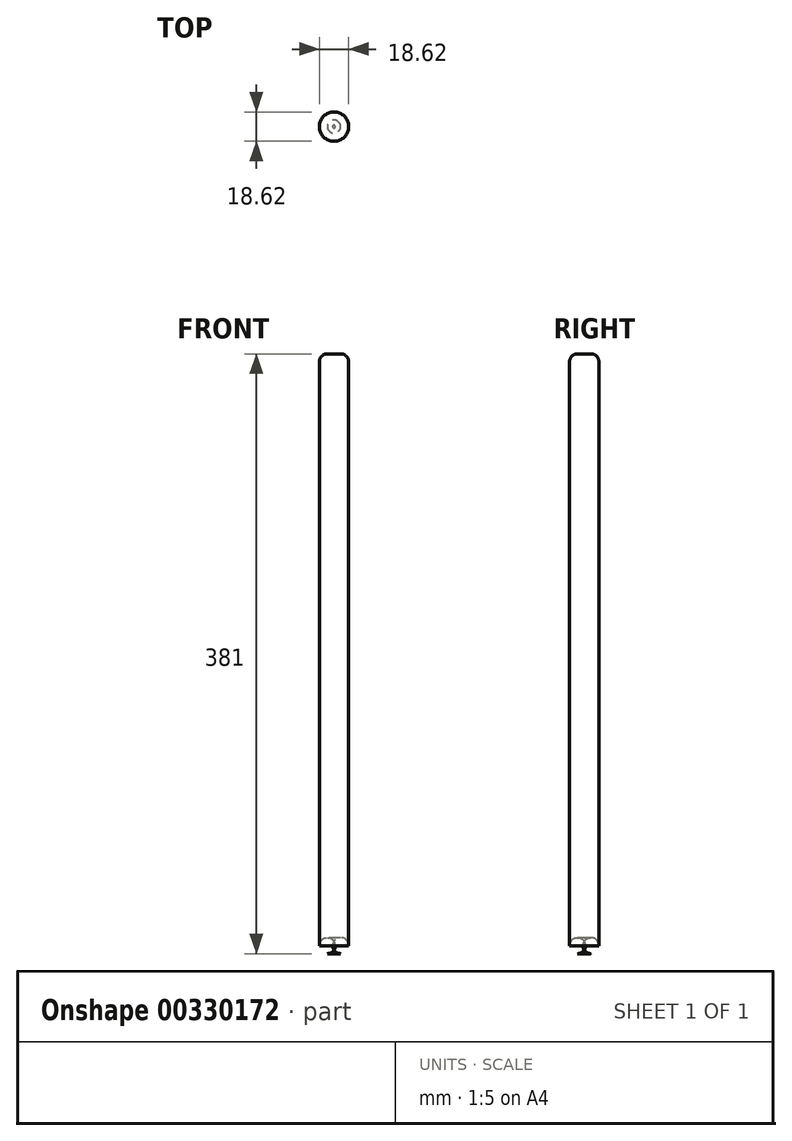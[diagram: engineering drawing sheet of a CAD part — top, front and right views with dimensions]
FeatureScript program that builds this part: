
annotation { "Feature Type Name" : "Feature", "Feature Type Description" : "" }
export const myFeature = defineFeature(function(context is Context, id is Id, definition is map)
    precondition{}
    {
        {
            var Q0;
            Q0=qCreatedBy(makeId("Top.planeOp"),FACE);
            var sketch = newSketch(context, id + "F0", { "sketchPlane" : qUnion([Q0])});
            skPoint(sketch, "E0", {"position": v(0, 0) * mm});
            skCircle(sketch, "E1", {"center": v(0, 0) * mm, "radius": 9.3 * mm});
            skSolve(sketch);
        }
        {
            var Q0;
            Q0 = qSketchRegion(id + "F0", true);
            extrude(context, id + "F1", {"entities" : qUnion([Q0]), "depth" : 381 * mm});
        }
        {
            var Q0;
            Q0=makeQuery(id+"F1.opExtrude","CAP_EDGE",EDGE,{"disambiguationData":[OSD([sQuery(id+"F0.wireOp",EDGE,"E1")])],"isStart":true});
            fillet(context, id + "F2", {"entities" : qUnion([Q0]), "radius" : 5.08 * mm, "tangentPropagation" : true, "allowEdgeOverflow" : false});
        }
        {
            var Q0;
            Q0=makeQuery(id+"F1.opExtrude","CAP_EDGE",EDGE,{"disambiguationData":[OSD([sQuery(id+"F0.wireOp",EDGE,"E1")])],"isStart":false});
            fillet(context, id + "F3", {"entities" : qUnion([Q0]), "radius" : 5.08 * mm, "tangentPropagation" : true, "allowEdgeOverflow" : false});
        }
    });
